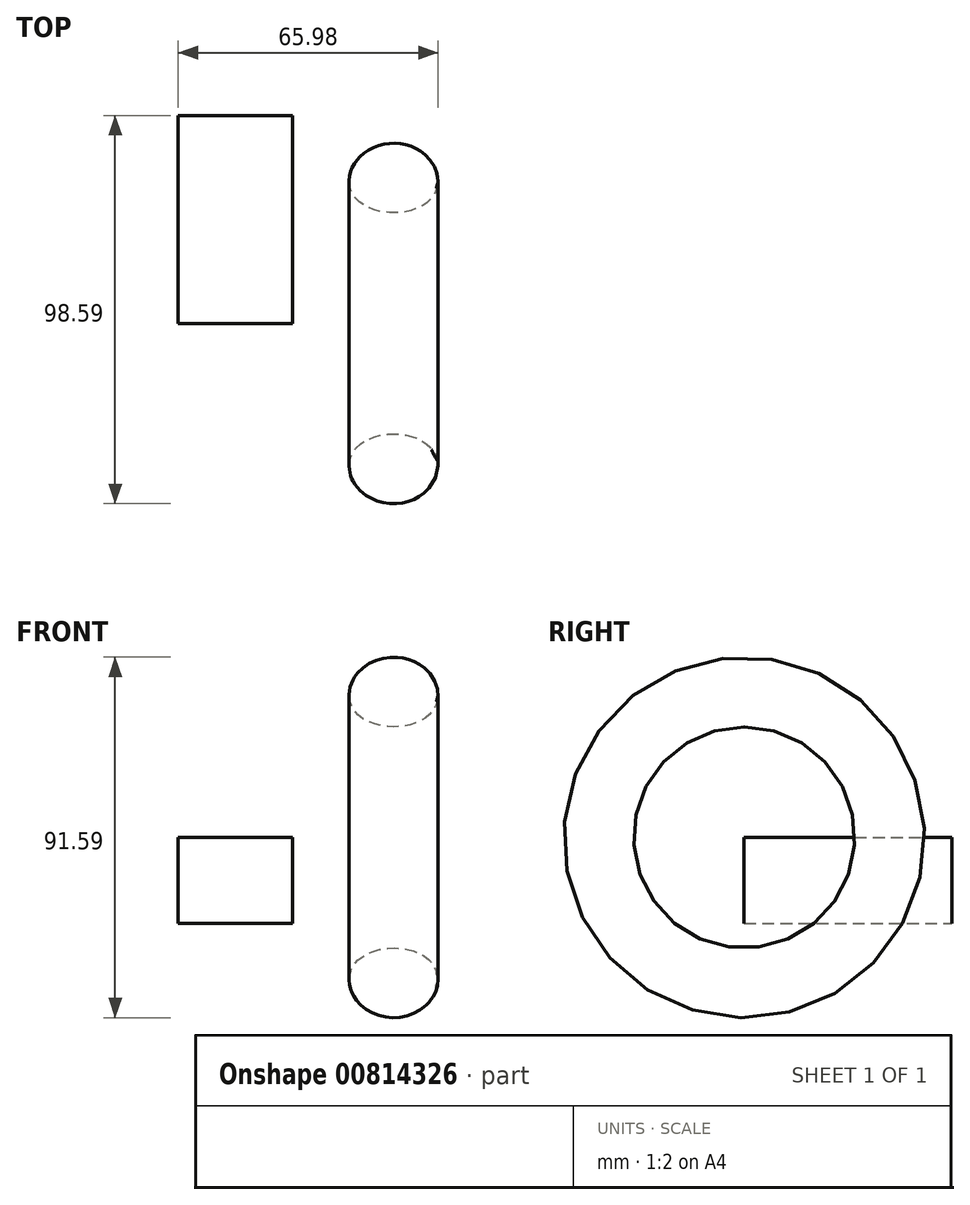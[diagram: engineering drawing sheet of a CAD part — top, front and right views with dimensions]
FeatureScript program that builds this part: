
annotation { "Feature Type Name" : "Feature", "Feature Type Description" : "" }
export const myFeature = defineFeature(function(context is Context, id is Id, definition is map)
    precondition{}
    {
        {
            var Q0;
            Q0=qCreatedBy(makeId("Top.planeOp"),FACE);
            var sketch = newSketch(context, id + "F0", { "sketchPlane" : qUnion([Q0])});
            skLineSegment(sketch, "E0.bottom", {"start": v(-10.27, -12) * mm, "end": v(18.76, -12) * mm});
            skLineSegment(sketch, "E0.top", {"start": v(-10.27, 40.8) * mm, "end": v(18.76, 40.8) * mm});
            skLineSegment(sketch, "E0.left", {"start": v(-10.27, -12) * mm, "end": v(-10.27, 40.8) * mm});
            skLineSegment(sketch, "E0.right", {"start": v(18.76, -12) * mm, "end": v(18.76, 40.8) * mm});
            skSolve(sketch);
        }
        {
            var Q0;
            Q0 = qSketchRegion(id + "F0", true);
            extrude(context, id + "F1", {"entities" : qUnion([Q0]), "depth" : 21.82 * mm, "offsetDistance" : 25 * mm});
        }
        {
            var Q0;
            Q0=qCreatedBy(makeId("Top.planeOp"),FACE);
            var sketch = newSketch(context, id + "F2", { "sketchPlane" : qUnion([Q0])});
            skCircle(sketch, "E1", {"center": v(44.43, 17) * mm, "radius": 11.27 * mm});
            skSolve(sketch);
        }
        {
            var Q0;
            Q0=makeQuery(id+"F2.imprint","IMPRINT",FACE,{"disambiguationData":[TD([[makeQuery(id+"F2.imprint","IMPRINT",EDGE,{"derivedFrom":sQuery(id+"F2.wireOp",EDGE,"E1")}),1.0]])]});
            var Q1;
            Q1=makeQuery(id+"F1.opExtrude","CAP_EDGE",EDGE,{"disambiguationData":[OSD([sQuery(id+"F0.wireOp",EDGE,"E0.bottom")])],"isStart":false});
            revolve(context, id + "F3", {"surfaceOperationType" : NewSurfaceOperationType.NEW, "entities" : qUnion([Q0]), "axis" : qUnion([Q1]), "revolveType" : RevolveType.FULL});
        }
    });
